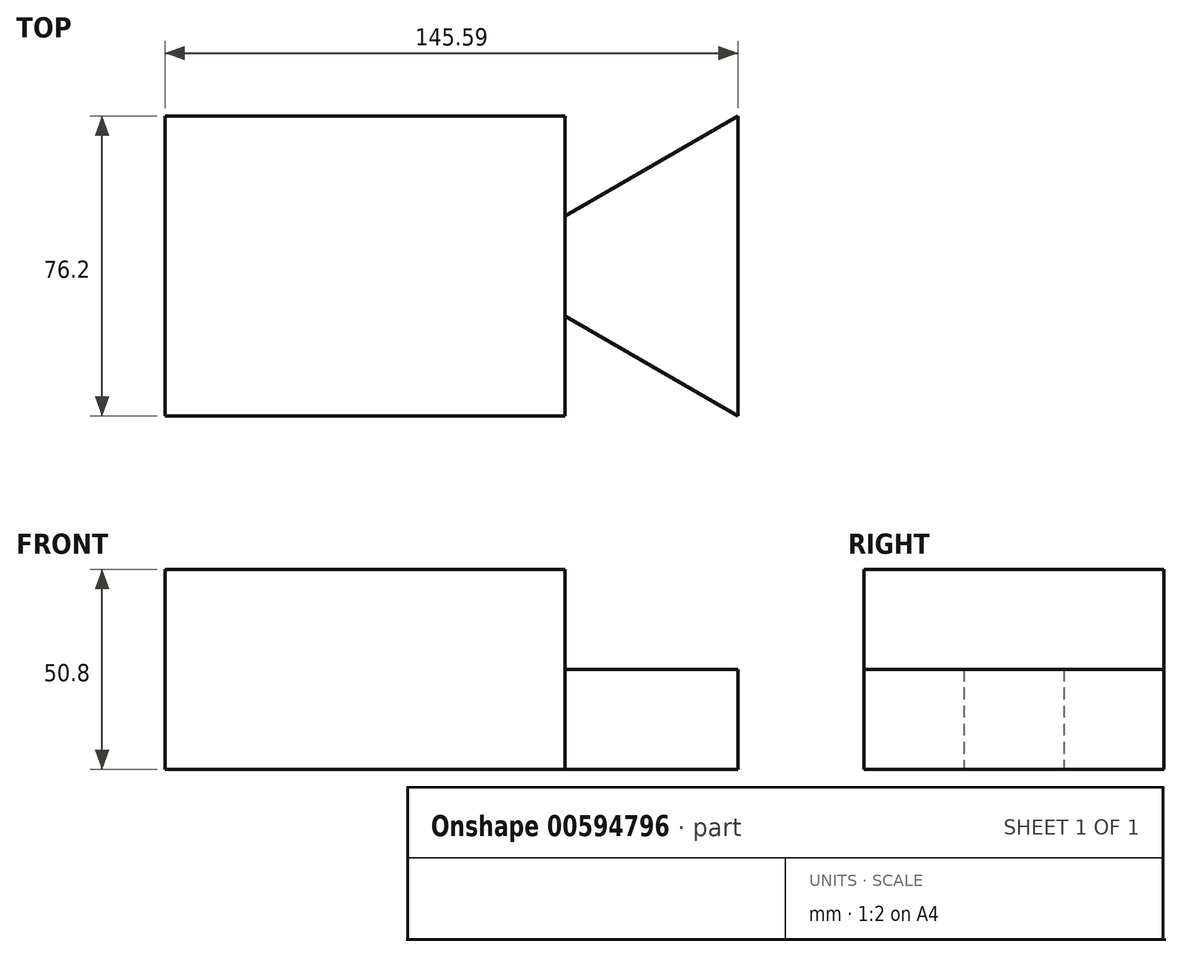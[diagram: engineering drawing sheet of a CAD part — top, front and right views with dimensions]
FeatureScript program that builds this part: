
annotation { "Feature Type Name" : "Feature", "Feature Type Description" : "" }
export const myFeature = defineFeature(function(context is Context, id is Id, definition is map)
    precondition{}
    {
        {
            var Q0;
            Q0=qCreatedBy(makeId("Top.planeOp"),FACE);
            var sketch = newSketch(context, id + "F0", { "sketchPlane" : qUnion([Q0])});
            skLineSegment(sketch, "E0.bottom", {"start": v(-51.13, 37) * mm, "end": v(50.47, 37) * mm});
            skLineSegment(sketch, "E0.top", {"start": v(-51.13, -39.2) * mm, "end": v(50.47, -39.2) * mm});
            skLineSegment(sketch, "E0.left", {"start": v(-51.13, 37) * mm, "end": v(-51.13, -39.2) * mm});
            skLineSegment(sketch, "E0.right", {"start": v(50.47, 37) * mm, "end": v(50.47, -39.2) * mm});
            skLineSegment(sketch, "E1", {"start": v(50.47, 11.6) * mm, "end": v(94.46, 37) * mm});
            skLineSegment(sketch, "E2", {"start": v(94.46, 37) * mm, "end": v(94.46, -39.2) * mm});
            skLineSegment(sketch, "E3", {"start": v(94.46, -39.2) * mm, "end": v(50.47, -13.8) * mm});
            skSolve(sketch);
        }
        {
            var Q0;
            {var subQ0=sQuery(id+"F0.wireOp",EDGE,"E1");Q0=makeQuery(id+"F0.imprint","IMPRINT",FACE,{"disambiguationData":[TD([[makeQuery(id+"F0.imprint","IMPRINT",EDGE,{"derivedFrom":subQ0}),-1.0]])]});}
            extrude(context, id + "F1", {"entities" : qUnion([Q0]), "depth" : 25.4 * mm, "offsetDistance" : 25.4 * mm});
        }
        {
            var Q0;
            {var subQ1=sQuery(id+"F0.wireOp",EDGE,"E0.bottom");Q0=makeQuery(id+"F0.imprint","IMPRINT",FACE,{"disambiguationData":[TD([[makeQuery(id+"F0.imprint","IMPRINT",EDGE,{"derivedFrom":subQ1}),-1.0]])]});}
            extrude(context, id + "F2", {"entities" : qUnion([Q0]), "operationType" : NewBodyOperationType.ADD, "depth" : 50.8 * mm, "offsetDistance" : 25.4 * mm});
        }
    });
